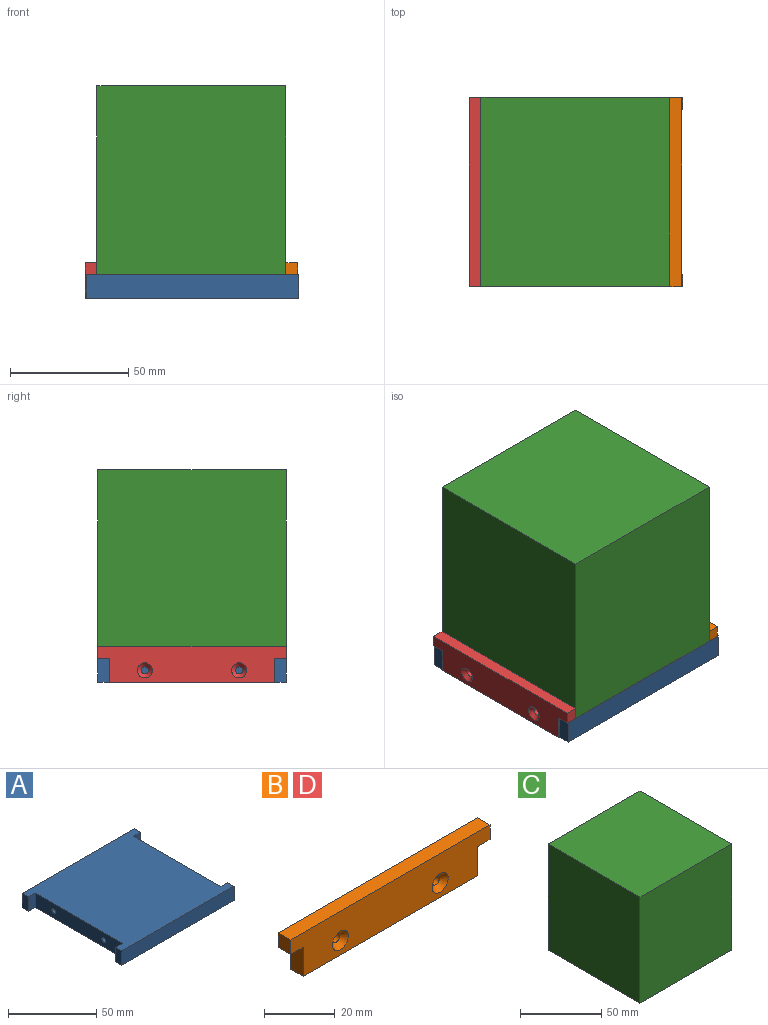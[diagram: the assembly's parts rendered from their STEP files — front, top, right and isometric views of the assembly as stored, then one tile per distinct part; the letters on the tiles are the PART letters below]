
ASSEMBLY  parts=4 mates=5
PART A: 26 faces, bbox 90x80x10 mm
  f0: plane 10x5mm, normal (-1,0,0), area 50mm2, adj f1,f11,f12,f13
  f1: plane 90x10mm, normal (0,-1,0), area 900mm2, adj f0,f2,f12,f13
  f2: plane 10x5mm, normal (1,0,0), area 50mm2, adj f1,f3,f12,f13
  f3: plane 10x5.5mm, normal (0,1,0), area 55mm2, adj f2,f4,f12,f13
  f4: plane 70x10mm, normal (1,0,0), area 685.9mm2, adj f3,f5,f12,f13,f18,f20
  f5: plane 10x5.5mm, normal (0,-1,0), area 55mm2, adj f4,f6,f12,f13
  f6: plane 10x5mm, normal (1,0,0), area 50mm2, adj f5,f7,f12,f13
  f7: plane 90x10mm, normal (0,1,0), area 900mm2, adj f6,f8,f12,f13
  f8: plane 10x5mm, normal (-1,0,0), area 50mm2, adj f7,f9,f12,f13
  f9: plane 10x5.5mm, normal (0,-1,0), area 55mm2, adj f8,f10,f12,f13
  f10: plane 70x10mm, normal (-1,0,0), area 685.9mm2, adj f9,f11,f12,f13,f22,f24
  f11: plane 10x5.5mm, normal (0,1,0), area 55mm2, adj f0,f10,f12,f13
  f12: plane 90x80mm, normal (0,0,1), area 6430mm2, adj f0,f1,f2,f3,f4,f5,f6,f7
  f13: plane 90x80mm, normal (0,0,-1), area 6404.9mm2, adj f0,f1,f2,f3,f4,f5,f6,f7
  f14: cylinder r=2mm len=7mm, axis (0,0,-1), area 88mm2, adj f13,f15
  f15: plane 4x4mm, normal (0,0,-1), area 12.6mm2, adj f14
  f16: cylinder r=2mm len=7mm, axis (0,0,-1), area 88mm2, adj f13,f17
  f17: plane 4x4mm, normal (0,0,-1), area 12.6mm2, adj f16
  f18: cylinder r=1.5mm len=15mm, axis (1,0,0), area 141.4mm2, adj f4,f19
  f19: plane 3x3mm, normal (1,0,0), area 7.1mm2, adj f18
  f20: cylinder r=1.5mm len=15mm, axis (1,0,0), area 141.4mm2, adj f4,f21
  f21: plane 3x3mm, normal (1,0,0), area 7.1mm2, adj f20
  f22: cylinder r=1.5mm len=15mm, axis (-1,0,0), area 141.4mm2, adj f10,f23
  f23: plane 3x3mm, normal (-1,0,0), area 7.1mm2, adj f22
  f24: cylinder r=1.5mm len=15mm, axis (-1,0,0), area 141.4mm2, adj f10,f25
  f25: plane 3x3mm, normal (-1,0,0), area 7.1mm2, adj f24
PART B: 14 faces, bbox 80x5x15.1 mm
  f0: plane 69.8x5mm, normal (0,0,-1), area 349mm2, adj f1,f8,f10,f11
  f1: plane 10.1x5mm, normal (1,0,0), area 50.5mm2, adj f0,f2,f10,f11
  f2: plane 5.1x5mm, normal (0,0,-1), area 25.5mm2, adj f1,f3,f10,f11
  f3: plane 5x5mm, normal (1,0,0), area 25mm2, adj f2,f4,f10,f11
  f4: plane 80x5mm, normal (0,0,1), area 400mm2, adj f3,f5,f10,f11
  f5: plane 5x5mm, normal (-1,0,0), area 25mm2, adj f4,f6,f10,f11
  f6: plane 5.1x5mm, normal (0,0,-1), area 25.5mm2, adj f5,f8,f10,f11
  f7: cylinder r=1.5mm len=3.3mm, axis (0,1,0), area 31.1mm2, adj f11,f13
  f8: plane 10.1x5mm, normal (-1,0,0), area 50.5mm2, adj f0,f6,f10,f11
  f9: cylinder r=1.5mm len=3.3mm, axis (0,1,0), area 31.1mm2, adj f11,f12
  f10: plane 80x15.1mm, normal (0,-1,0), area 1040.6mm2, adj f0,f1,f2,f3,f4,f5,f6,f8
  f11: plane 80x15.1mm, normal (0,1,0), area 1090.8mm2, adj f0,f1,f2,f3,f4,f5,f6,f7
  f12: cone r=1.5mm half-angle=45deg, axis (0,-1,0), area 35.5mm2, adj f9,f10
  f13: cone r=1.5mm half-angle=45deg, axis (0,-1,0), area 35.5mm2, adj f7,f10
PART C: 6 faces, bbox 80x80x80 mm
  f0: plane 80x80mm, normal (0,-1,0), area 6400mm2, adj f1,f3,f4,f5
  f1: plane 80x80mm, normal (1,0,0), area 6400mm2, adj f0,f2,f4,f5
  f2: plane 80x80mm, normal (0,1,0), area 6400mm2, adj f1,f3,f4,f5
  f3: plane 80x80mm, normal (-1,0,0), area 6400mm2, adj f0,f2,f4,f5
  f4: plane 80x80mm, normal (0,0,1), area 6400mm2, adj f0,f1,f2,f3
  f5: plane 80x80mm, normal (0,0,-1), area 6400mm2, adj f0,f1,f2,f3
PART D: same geometry as B
PLACE A t=(3.36,-3.96,-22)mm
PLACE B rot(axis=(0,0,1),90deg) t=(42.86,-3.96,-22)mm
PLACE C t=(2.86,-3.96,-12)mm
PLACE D rot(axis=(0,0,-1),90deg) t=(-37.14,-3.96,-22)mm
MATE planar D.f0 <-> A.f13  axis (0,0,-1) through (-39.64,-3.96,-22)mm
MATE planar B.f0 <-> A.f13  axis (0,0,-1) through (45.36,-3.96,-22)mm
MATE planar D.f11 <-> C.f3  axis (1,0,0) through (-37.14,-3.96,-14.18)mm
MATE planar B.f11 <-> C.f1  axis (-1,0,0) through (42.86,-3.96,-14.18)mm
MATE planar C.f5 <-> A.f12  axis (0,0,-1) through (2.86,-3.96,-12)mm
